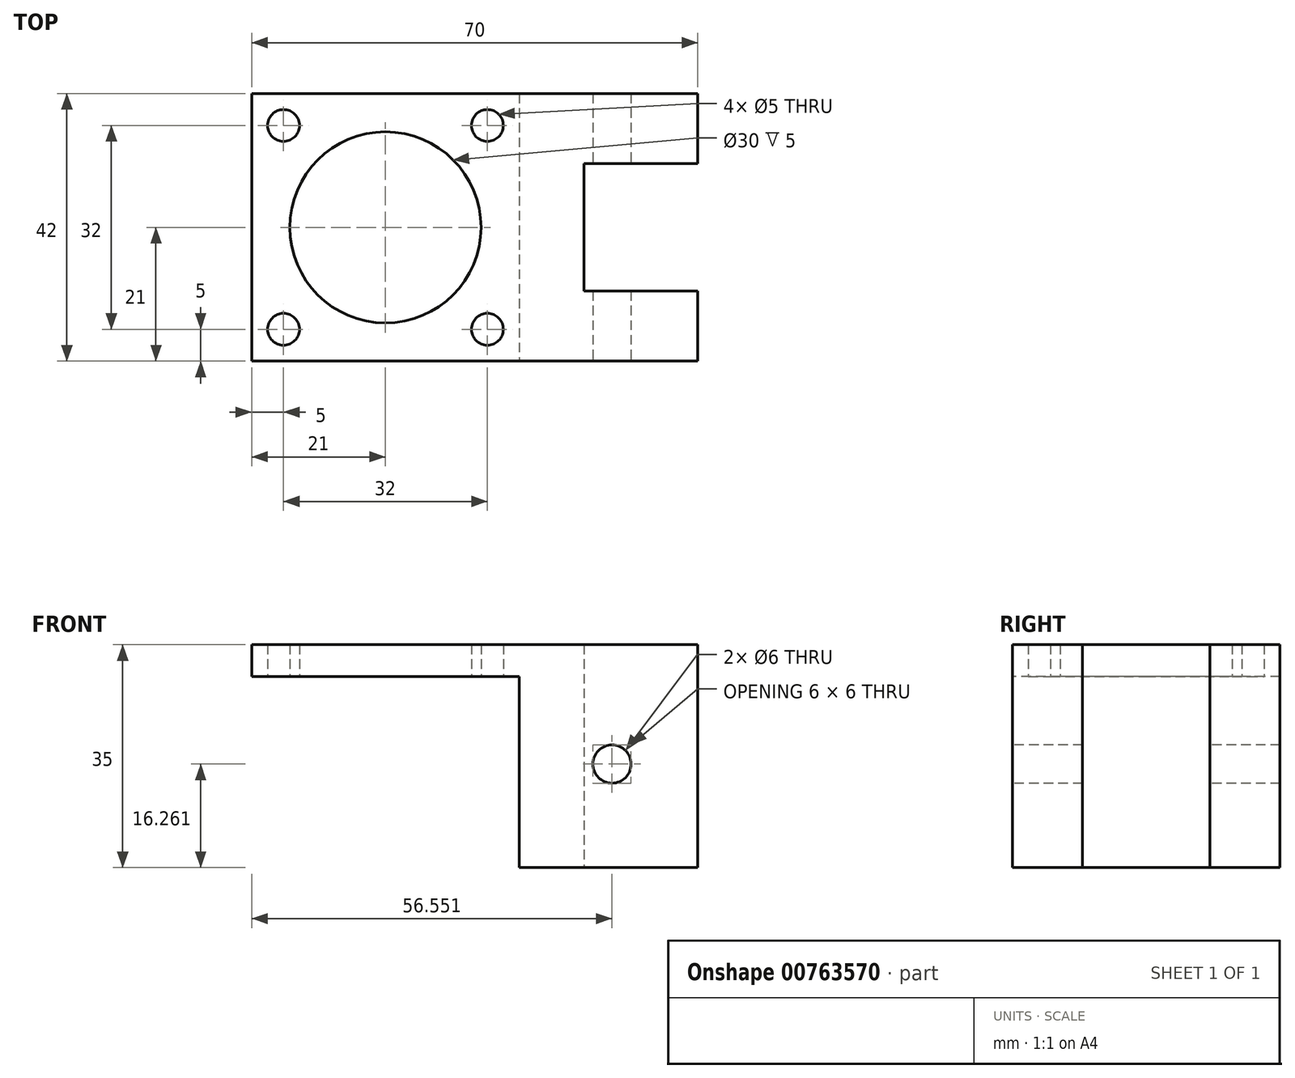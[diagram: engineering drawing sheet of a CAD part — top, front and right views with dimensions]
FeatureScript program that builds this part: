
annotation { "Feature Type Name" : "Feature", "Feature Type Description" : "" }
export const myFeature = defineFeature(function(context is Context, id is Id, definition is map)
    precondition{}
    {
        {
            var Q0;
            Q0=qCreatedBy(makeId("Top.planeOp"),FACE);
            var sketch = newSketch(context, id + "F0", { "sketchPlane" : qUnion([Q0])});
            skLineSegment(sketch, "E0.bottom", {"start": v(21, 21) * mm, "end": v(-21, 21) * mm});
            skLineSegment(sketch, "E0.top", {"start": v(21, -21) * mm, "end": v(-21, -21) * mm});
            skLineSegment(sketch, "E0.left", {"start": v(21, 21) * mm, "end": v(21, -21) * mm});
            skLineSegment(sketch, "E0.right", {"start": v(-21, 21) * mm, "end": v(-21, -21) * mm});
            skPoint(sketch, "E0.middle", {"position": v(0, 0) * mm});
            skLineSegment(sketch, "E1.bottom", {"start": v(21, 21) * mm, "end": v(49, 21) * mm});
            skLineSegment(sketch, "E1.top", {"start": v(21, -21) * mm, "end": v(49, -21) * mm});
            skLineSegment(sketch, "E1.right", {"start": v(49, 21) * mm, "end": v(49, -21) * mm});
            skLineSegment(sketch, "E2.0", {"start": v(16, 16) * mm, "end": v(-16, 16) * mm, "construction": true});
            skLineSegment(sketch, "E2.1", {"start": v(16, 16) * mm, "end": v(16, -16) * mm, "construction": true});
            skLineSegment(sketch, "E2.2", {"start": v(16, -16) * mm, "end": v(-16, -16) * mm, "construction": true});
            skLineSegment(sketch, "E2.3", {"start": v(-16, 16) * mm, "end": v(-16, -16) * mm, "construction": true});
            skCircle(sketch, "E3", {"center": v(-16, 16) * mm, "radius": 2.5 * mm});
            skCircle(sketch, "E4", {"center": v(16, 16) * mm, "radius": 2.5 * mm});
            skCircle(sketch, "E5", {"center": v(-16, -16) * mm, "radius": 2.5 * mm});
            skCircle(sketch, "E6", {"center": v(16, -16) * mm, "radius": 2.5 * mm});
            skLineSegment(sketch, "E7", {"start": v(35, 21) * mm, "end": v(35, -21) * mm, "construction": true});
            skLineSegment(sketch, "E8.direction1", {"start": v(35, 0) * mm, "end": v(60, 0) * mm, "construction": true});
            skLineSegment(sketch, "E9", {"start": v(49, 10) * mm, "end": v(21, 10) * mm, "construction": true});
            skLineSegment(sketch, "E10", {"start": v(21, -10) * mm, "end": v(49, -10) * mm, "construction": true});
            skLineSegment(sketch, "E11", {"start": v(31.12, 10) * mm, "end": v(31.12, -10) * mm});
            skCircle(sketch, "E12", {"center": v(0, 0) * mm, "radius": 15 * mm});
            skLineSegment(sketch, "E13", {"start": v(31.12, 10) * mm, "end": v(49, 10) * mm});
            skLineSegment(sketch, "E14", {"start": v(31.12, -10) * mm, "end": v(49, -10) * mm});
            skSolve(sketch);
        }
        {
            var Q0;
            Q0=makeQuery(id+"F0.imprint","IMPRINT",FACE,{"disambiguationData":[TD([[makeQuery(id+"F0.imprint","IMPRINT",EDGE,{"derivedFrom":sQuery(id+"F0.wireOp",EDGE,"E0.bottom")}),1.0]])]});
            extrude(context, id + "F1", {"entities" : qUnion([Q0]), "depth" : 5 * mm, "offsetDistance" : 25 * mm});
        }
        {
            var Q0;
            Q0=makeQuery(id+"F0.imprint","IMPRINT",FACE,{"disambiguationData":[TD([[makeQuery(id+"F0.imprint","IMPRINT",EDGE,{"derivedFrom":sQuery(id+"F0.wireOp",EDGE,"E1.bottom")}),-1.0]])]});
            extrude(context, id + "F2", {"entities" : qUnion([Q0]), "operationType" : NewBodyOperationType.ADD, "depth" : 5 * mm, "offsetDistance" : 25 * mm, "hasSecondDirection" : true, "secondDirectionOppositeDirection" : true, "secondDirectionDepth" : 30 * mm});
        }
        {
            var Q0;
            Q0=makeQuery(id+"F2.boolean.opBoolean","MERGE",FACE,{"derivedFrom":[makeQuery(id+"F1.opExtrude","SWEPT_FACE",FACE,{"disambiguationData":[OSD([sQuery(id+"F0.wireOp",EDGE,"E0.top")])]}),makeQuery(id+"F2.opExtrude","SWEPT_FACE",FACE,{"disambiguationData":[OSD([sQuery(id+"F0.wireOp",EDGE,"E1.top")])]})]});
            var sketch = newSketch(context, id + "F3", { "sketchPlane" : qUnion([Q0])});
            skCircle(sketch, "E15", {"center": v(35.55, -13.74) * mm, "radius": 3 * mm});
            skSolve(sketch);
        }
        {
            var Q0;
            Q0 = qSketchRegion(id + "F3", true);
            extrude(context, id + "F4", {"entities" : qUnion([Q0]), "operationType" : NewBodyOperationType.REMOVE, "oppositeDirection" : true, "depth" : 50 * mm, "offsetDistance" : 25 * mm});
        }
    });
